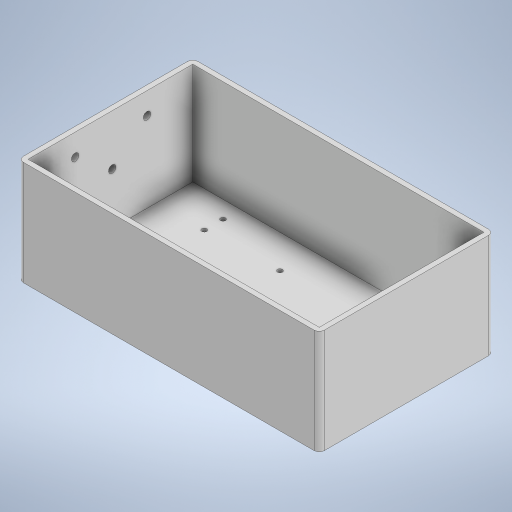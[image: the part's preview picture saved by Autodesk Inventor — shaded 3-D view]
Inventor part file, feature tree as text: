
AUTODESK INVENTOR PART (.ipt)
format: ipt  version: 2023 (Build 270158030, 158C)  size: 508,928 bytes
history: native  units: mm
features: other x4, extrude x4, sketch x4
ambient origin geometry x8: Origin, YZ Plane, XZ Plane, XY Plane, X Axis, Y Axis, Z Axis, Center Point
bodies: Body1 (feature_tree), Body2 (feature_tree)
feature tree (12):
  other  "Kepler_Vibe_XL.iam"
  other  "Die Cast Box.ipt:1"
  other  "Vibe Enclosure"
  extrude  "Extrusion1"  Depth=2.0mm
  extrude  "Extrusion2"  Depth=2.0mm
  extrude  "Extrusion3"  Depth=2.0mm
  extrude  "Extrusion4"  Depth=2.0mm
  sketch  "Sketch1"  dims[d0=10.0mm d1=2.0mm]
  other  "Drill Jig"
  sketch  "Sketch2"  dims[d2=2.0mm d3=2.0mm]
  sketch  "Sketch3"  dims[d4=2.0mm d5=2.0mm]
  sketch  "Sketch4"  dims[d6=2.0mm d7=2.0mm d8=2.0mm d9=2.0mm d10=2.0mm d11=0.0mm d12=2.0mm d13=2.0mm d14=2.0mm d15=2.0mm d16=2.0mm d17=40.0mm d18=0.0mm d19=2.0mm d20=2.0mm d21=2.0mm d22=2.0mm d23=40.0mm d24=-0.261799mm d25=3.0mm d26=3.0mm d27=50.0mm d28=0.0mm]
